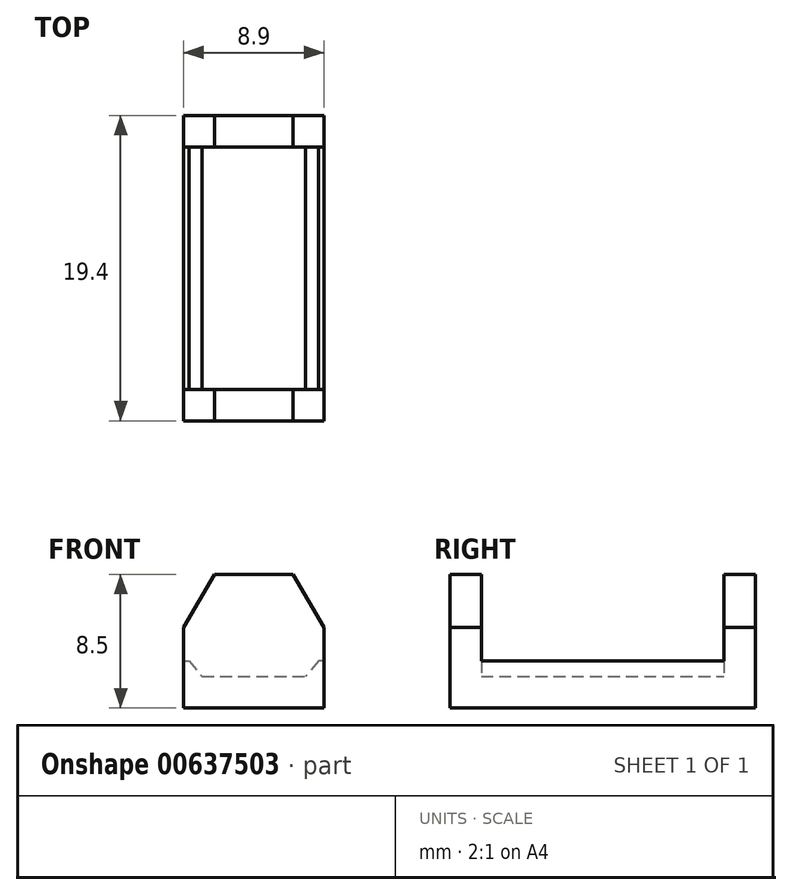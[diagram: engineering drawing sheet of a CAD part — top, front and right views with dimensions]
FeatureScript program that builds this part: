
annotation { "Feature Type Name" : "Feature", "Feature Type Description" : "" }
export const myFeature = defineFeature(function(context is Context, id is Id, definition is map)
    precondition{}
    {
        {
            var Q0;
            Q0=qCreatedBy(makeId("Front.planeOp"),FACE);
            var sketch = newSketch(context, id + "F0", { "sketchPlane" : qUnion([Q0])});
            skLineSegment(sketch, "E0", {"start": v(0, 0) * mm, "end": v(0, 8.5) * mm, "construction": true});
            skLineSegment(sketch, "E1", {"start": v(0, 8.5) * mm, "end": v(2.5, 8.5) * mm});
            skLineSegment(sketch, "E2", {"start": v(2.5, 8.5) * mm, "end": v(4.45, 5.12) * mm});
            skLineSegment(sketch, "E3", {"start": v(4.45, 5.12) * mm, "end": v(4.45, 0) * mm});
            skLineSegment(sketch, "E4", {"start": v(4.45, 0) * mm, "end": v(0, 0) * mm});
            skLineSegment(sketch, "E5.MirrorCS", {"start": v(0, 8.5) * mm, "end": v(-2.5, 8.5) * mm});
            skLineSegment(sketch, "E6.MirrorCS", {"start": v(-4.45, 5.12) * mm, "end": v(-4.45, 0) * mm});
            skLineSegment(sketch, "E7.MirrorCS", {"start": v(-4.45, 0) * mm, "end": v(0, 0) * mm});
            skLineSegment(sketch, "E8.MirrorCS", {"start": v(-2.5, 8.5) * mm, "end": v(-4.45, 5.12) * mm});
            skSolve(sketch);
        }
        {
            var Q0;
            Q0=makeQuery(id+"F0.imprint","IMPRINT",FACE,{"disambiguationData":[TD([[makeQuery(id+"F0.imprint","IMPRINT",EDGE,{"derivedFrom":sQuery(id+"F0.wireOp",EDGE,"E1")}),-1.0]])]});
            extrude(context, id + "F1", {"entities" : qUnion([Q0]), "depth" : 9.7 * mm, "offsetDistance" : 25 * mm});
        }
        {
            var Q0;
            Q0=qCreatedBy(makeId("Front.planeOp"),FACE);
            var sketch = newSketch(context, id + "F2", { "sketchPlane" : qUnion([Q0])});
            skLineSegment(sketch, "E9", {"start": v(-4.45, 3) * mm, "end": v(-4.12, 3) * mm});
            skLineSegment(sketch, "E10", {"start": v(-4.12, 3) * mm, "end": v(-3.28, 2) * mm});
            skLineSegment(sketch, "E11", {"start": v(-3.28, 2) * mm, "end": v(0, 2) * mm});
            skLineSegment(sketch, "E12", {"start": v(-4.45, 3) * mm, "end": v(-4.45, 5.12) * mm});
            skLineSegment(sketch, "E13", {"start": v(-4.45, 5.12) * mm, "end": v(-2.5, 8.5) * mm});
            skLineSegment(sketch, "E14", {"start": v(-2.5, 8.5) * mm, "end": v(0, 8.5) * mm});
            skLineSegment(sketch, "E15", {"start": v(0, 0) * mm, "end": v(0, 8.5) * mm});
            skLineSegment(sketch, "E16.MirrorCS", {"start": v(4.45, 3) * mm, "end": v(4.12, 3) * mm});
            skLineSegment(sketch, "E17.MirrorCS", {"start": v(4.12, 3) * mm, "end": v(3.28, 2) * mm});
            skLineSegment(sketch, "E18.MirrorCS", {"start": v(4.45, 5.12) * mm, "end": v(2.5, 8.5) * mm});
            skLineSegment(sketch, "E19.MirrorCS", {"start": v(3.28, 2) * mm, "end": v(0, 2) * mm});
            skLineSegment(sketch, "E20.MirrorCS", {"start": v(2.5, 8.5) * mm, "end": v(0, 8.5) * mm});
            skLineSegment(sketch, "E21.MirrorCS", {"start": v(4.45, 3) * mm, "end": v(4.45, 5.12) * mm});
            skSolve(sketch);
        }
        {
            var Q0;
            Q0 = qSketchRegion(id + "F2", true);
            var Q1;
            Q1=makeQuery(id+"F1.opExtrude","CAP_FACE",FACE,{"disambiguationData":[OSD([sQuery(id+"F0.wireOp",EDGE,"E1"),sQuery(id+"F0.wireOp",EDGE,"E2"),sQuery(id+"F0.wireOp",EDGE,"E3"),sQuery(id+"F0.wireOp",EDGE,"E4"),sQuery(id+"F0.wireOp",EDGE,"E5.MirrorCS"),sQuery(id+"F0.wireOp",EDGE,"E6.MirrorCS"),sQuery(id+"F0.wireOp",EDGE,"E7.MirrorCS"),sQuery(id+"F0.wireOp",EDGE,"E8.MirrorCS")])],"isStart":false});
            extrude(context, id + "F3", {"entities" : qUnion([Q0]), "operationType" : NewBodyOperationType.REMOVE, "endBound" : BoundingType.UP_TO_SURFACE, "depth" : 8.04 * mm, "endBoundEntityFace" : qUnion([Q1]), "hasOffset" : true, "offsetDistance" : 2 * mm});
        }
        {
            var Q0;
            Q0=makeQuery(id+"F1.opExtrude","SWEPT_BODY",BODY,{"disambiguationData":[OSD([sQuery(id+"F0.wireOp",EDGE,"E1"),sQuery(id+"F0.wireOp",EDGE,"E2"),sQuery(id+"F0.wireOp",EDGE,"E3"),sQuery(id+"F0.wireOp",EDGE,"E4"),sQuery(id+"F0.wireOp",EDGE,"E5.MirrorCS"),sQuery(id+"F0.wireOp",EDGE,"E6.MirrorCS"),sQuery(id+"F0.wireOp",EDGE,"E7.MirrorCS"),sQuery(id+"F0.wireOp",EDGE,"E8.MirrorCS")])]});
            var Q1;
            Q1=qCreatedBy(makeId("Front.planeOp"),FACE);
            mirror(context, id + "F4", {"operationType" : NewBodyOperationType.ADD, "entities" : qUnion([Q0]), "mirrorPlane" : qUnion([Q1])});
        }
    });
